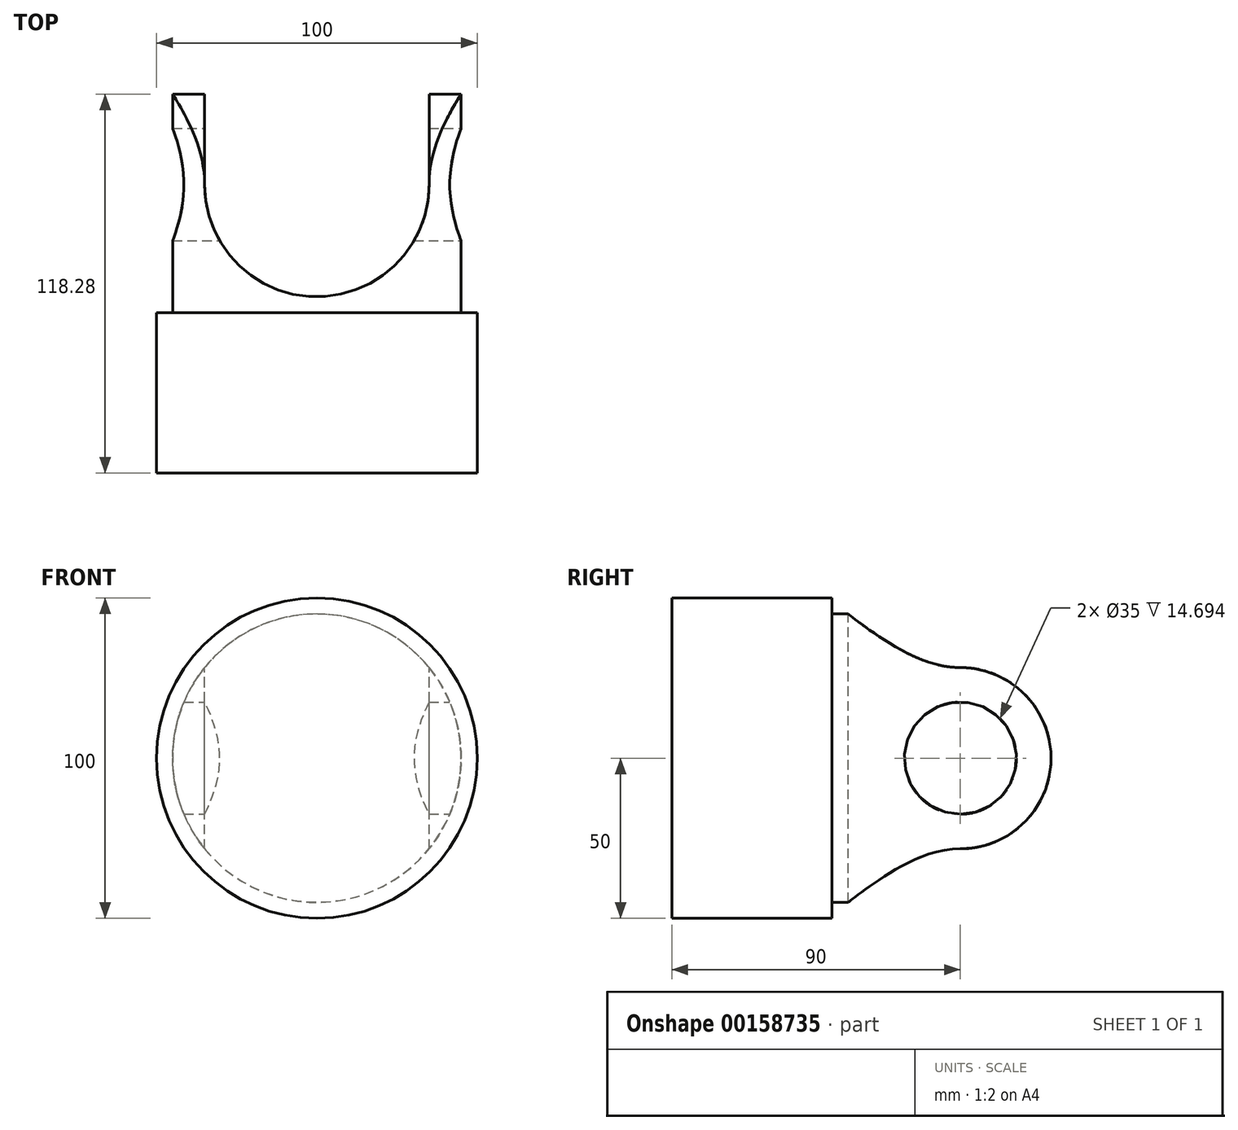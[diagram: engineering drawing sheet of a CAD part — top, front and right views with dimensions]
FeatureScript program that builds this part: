
annotation { "Feature Type Name" : "Feature", "Feature Type Description" : "" }
export const myFeature = defineFeature(function(context is Context, id is Id, definition is map)
    precondition{}
    {
        {
            var Q0;
            Q0=qCreatedBy(makeId("Front.planeOp"),FACE);
            var sketch = newSketch(context, id + "F0", { "sketchPlane" : qUnion([Q0])});
            skCircle(sketch, "E0", {"center": v(0, 0) * mm, "radius": 50 * mm});
            skSolve(sketch);
        }
        {
            var Q0;
            Q0 = qSketchRegion(id + "F0", true);
            extrude(context, id + "F1", {"entities" : qUnion([Q0]), "oppositeDirection" : true, "depth" : 50 * mm});
        }
        {
            var Q0;
            Q0=makeQuery(id+"F1.opExtrude","CAP_FACE",FACE,{"disambiguationData":[OSD([sQuery(id+"F0.wireOp",EDGE,"E0")])],"isStart":false});
            var sketch = newSketch(context, id + "F2", { "sketchPlane" : qUnion([Q0])});
            skCircle(sketch, "E1", {"center": v(0, 0) * mm, "radius": 45 * mm});
            skSolve(sketch);
        }
        {
            var Q0;
            Q0 = qSketchRegion(id + "F2", true);
            extrude(context, id + "F3", {"entities" : qUnion([Q0]), "operationType" : NewBodyOperationType.ADD, "depth" : 80 * mm});
        }
        {
            var Q0;
            Q0=qCreatedBy(makeId("Top.planeOp"),FACE);
            var sketch = newSketch(context, id + "F4", { "sketchPlane" : qUnion([Q0])});
            skCircle(sketch, "E2", {"center": v(0, 90) * mm, "radius": 35 * mm});
            skLineSegment(sketch, "E3", {"start": v(35, 90) * mm, "end": v(35, 130) * mm});
            skPoint(sketch, "E4", {"position": v(-35, 90) * mm});
            skLineSegment(sketch, "E5", {"start": v(-35, 90) * mm, "end": v(-35, 130) * mm});
            skLineSegment(sketch, "E6", {"start": v(-35, 130) * mm, "end": v(35, 130) * mm});
            skSolve(sketch);
        }
        {
            var Q0;
            Q0 = qSketchRegion(id + "F4", true);
            extrude(context, id + "F5", {"entities" : qUnion([Q0]), "operationType" : NewBodyOperationType.REMOVE, "endBound" : BoundingType.SYMMETRIC, "oppositeDirection" : true, "depth" : 200 * mm});
        }
        {
            var Q0;
            Q0=makeQuery(id+"F5.boolean.opBoolean","COPY",FACE,{"derivedFrom":makeQuery(id+"F5.opExtrude","SWEPT_FACE",FACE,{"disambiguationData":[OSD([sQuery(id+"F4.wireOp",EDGE,"E5")])]})});
            var sketch = newSketch(context, id + "F6", { "sketchPlane" : qUnion([Q0])});
            skCircle(sketch, "E7", {"center": v(90, 0) * mm, "radius": 17.5 * mm});
            skArc(sketch, "E8", {"start": v(90, -28.28) * mm, "mid": v(118.28, 0) * mm, "end": v(90, 28.28) * mm});
            skLineSegment(sketch, "E9", {"start": v(90, 28.28) * mm, "end": v(130, 28.28) * mm});
            skLineSegment(sketch, "E10", {"start": v(130, 28.28) * mm, "end": v(130, -28.28) * mm});
            skLineSegment(sketch, "E11", {"start": v(130, -28.28) * mm, "end": v(90, -28.28) * mm});
            skSolve(sketch);
        }
        {
            var Q0;
            Q0 = qSketchRegion(id + "F6", true);
            extrude(context, id + "F7", {"entities" : qUnion([Q0]), "operationType" : NewBodyOperationType.REMOVE, "endBound" : BoundingType.SYMMETRIC, "oppositeDirection" : true, "depth" : 200 * mm});
        }
    });
